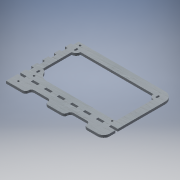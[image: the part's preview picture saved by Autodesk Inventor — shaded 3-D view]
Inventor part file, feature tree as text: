
AUTODESK INVENTOR PART (.ipt)
format: ipt  version: 2018.3 (Build 223284000, 284)  size: 252,416 bytes
history: native  units: mm
features: reference x16, other x5, extrude x3, sketch x3, fillet x2
ambient origin geometry x8: Origin, YZ Plane, XZ Plane, XY Plane, X Axis, Y Axis, Z Axis, Center Point
bodies: Solido1 (feature_tree)
feature tree (29):
  extrude  "Estrusione1"  Depth=165.0mm
  extrude  "Estrusione2"  Depth=33.0mm
  fillet  "Raccordo1"  Radius=10.0mm
  fillet  "Raccordo2"  Radius=33.0mm
  extrude  "Estrusione3"  Depth=10.0mm
  sketch  "Schizzo1"
  reference  "Riferimento4"
  reference  "Riferimento5"
  reference  "Riferimento6"
  reference  "Riferimento8"
  reference  "Riferimento9"
  reference  "Riferimento10"
  reference  "Riferimento11"
  reference  "Riferimento12"
  reference  "Riferimento13"
  reference  "Riferimento14"
  reference  "Riferimento15"
  sketch  "Schizzo2"
  sketch  "Schizzo3"
  reference  "Riferimento16"
  reference  "Riferimento17"
  reference  "Riferimento18"
  reference  "Riferimento19"
  reference  "Riferimento20"
  other  "<userpath>\Desktop\Scorbot Hardware\Case Board V2\caseHw v2.iam"
  other  "caseHw v2.iam"
  other  "LC600H-12:1"
  other  "tavolaBase:1"
  other  "Dietro:1"
